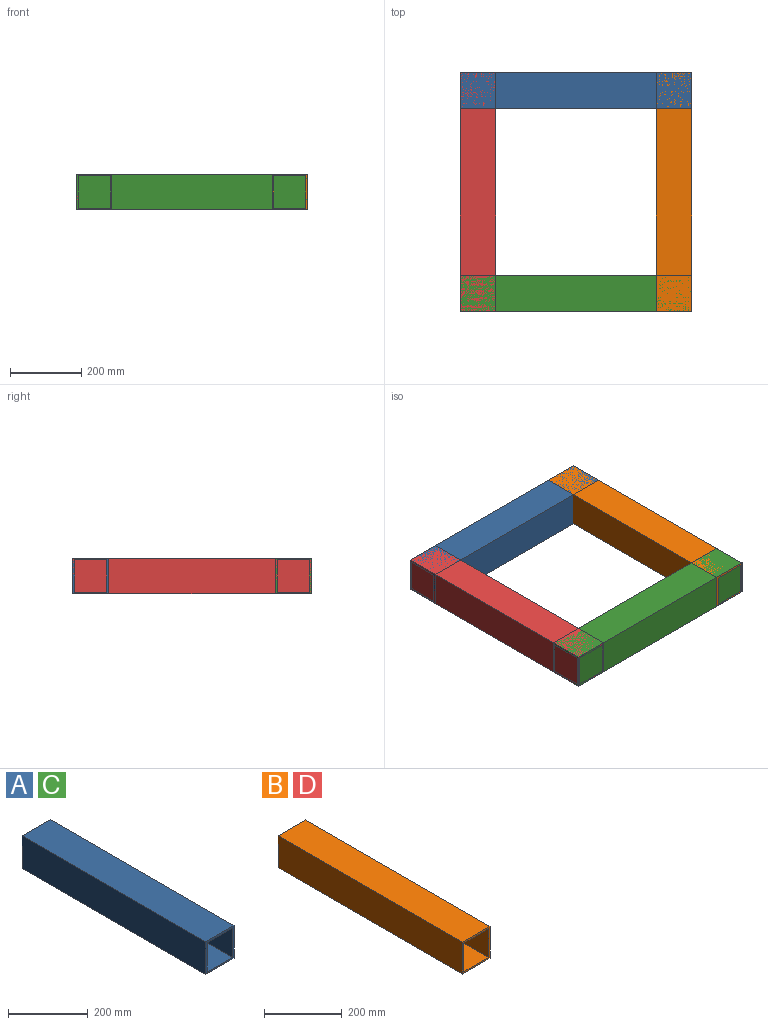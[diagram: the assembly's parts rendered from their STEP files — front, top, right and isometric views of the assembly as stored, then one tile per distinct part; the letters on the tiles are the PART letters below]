
ASSEMBLY  parts=4 mates=3
PART A: 10 faces, bbox 100x650x100 mm
  f0: plane 650x90mm, normal (1,0,0), area 58500mm2, adj f1,f7,f8,f9
  f1: plane 650x90mm, normal (0,0,-1), area 58500mm2, adj f0,f2,f8,f9
  f2: plane 650x90mm, normal (-1,0,0), area 58500mm2, adj f1,f7,f8,f9
  f3: plane 650x100mm, normal (-1,0,0), area 65000mm2, adj f4,f6,f8,f9
  f4: plane 650x100mm, normal (0,0,-1), area 65000mm2, adj f3,f5,f8,f9
  f5: plane 650x100mm, normal (1,0,0), area 65000mm2, adj f4,f6,f8,f9
  f6: plane 650x100mm, normal (0,0,1), area 65000mm2, adj f3,f5,f8,f9
  f7: plane 650x90mm, normal (0,0,1), area 58500mm2, adj f0,f2,f8,f9
  f8: plane 100x100mm, normal (0,-1,0), area 1900mm2, adj f0,f1,f2,f3,f4,f5,f6,f7
  f9: plane 100x100mm, normal (0,1,0), area 1900mm2, adj f0,f1,f2,f3,f4,f5,f6,f7
PART B: 10 faces, bbox 100x670x100 mm
  f0: plane 670x90mm, normal (1,0,0), area 60300mm2, adj f1,f7,f8,f9
  f1: plane 670x90mm, normal (0,0,-1), area 60300mm2, adj f0,f2,f8,f9
  f2: plane 670x90mm, normal (-1,0,0), area 60300mm2, adj f1,f7,f8,f9
  f3: plane 670x100mm, normal (-1,0,0), area 67000mm2, adj f4,f6,f8,f9
  f4: plane 670x100mm, normal (0,0,-1), area 67000mm2, adj f3,f5,f8,f9
  f5: plane 670x100mm, normal (1,0,0), area 67000mm2, adj f4,f6,f8,f9
  f6: plane 670x100mm, normal (0,0,1), area 67000mm2, adj f3,f5,f8,f9
  f7: plane 670x90mm, normal (0,0,1), area 60300mm2, adj f0,f2,f8,f9
  f8: plane 100x100mm, normal (0,-1,0), area 1900mm2, adj f0,f1,f2,f3,f4,f5,f6,f7
  f9: plane 100x100mm, normal (0,1,0), area 1900mm2, adj f0,f1,f2,f3,f4,f5,f6,f7
PART C: same geometry as A
PART D: same geometry as B
PLACE A rot(axis=(0,0,1),90deg) t=(-41.5,-28.98,20.32)mm
PLACE B t=(508.5,71.02,20.32)mm
PLACE C rot(axis=(0,0,1),90deg) t=(-41.5,-598.98,20.32)mm
PLACE D t=(-41.5,71.02,20.32)mm
MATE planar C.f6 <-> D.f6  axis (0,0,1) through (283.5,-548.98,120.32)mm
MATE planar B.f6 <-> D.f6  axis (0,0,1) through (558.5,-263.98,120.32)mm
MATE planar A.f6 <-> D.f6  axis (0,0,1) through (283.5,21.02,120.32)mm
